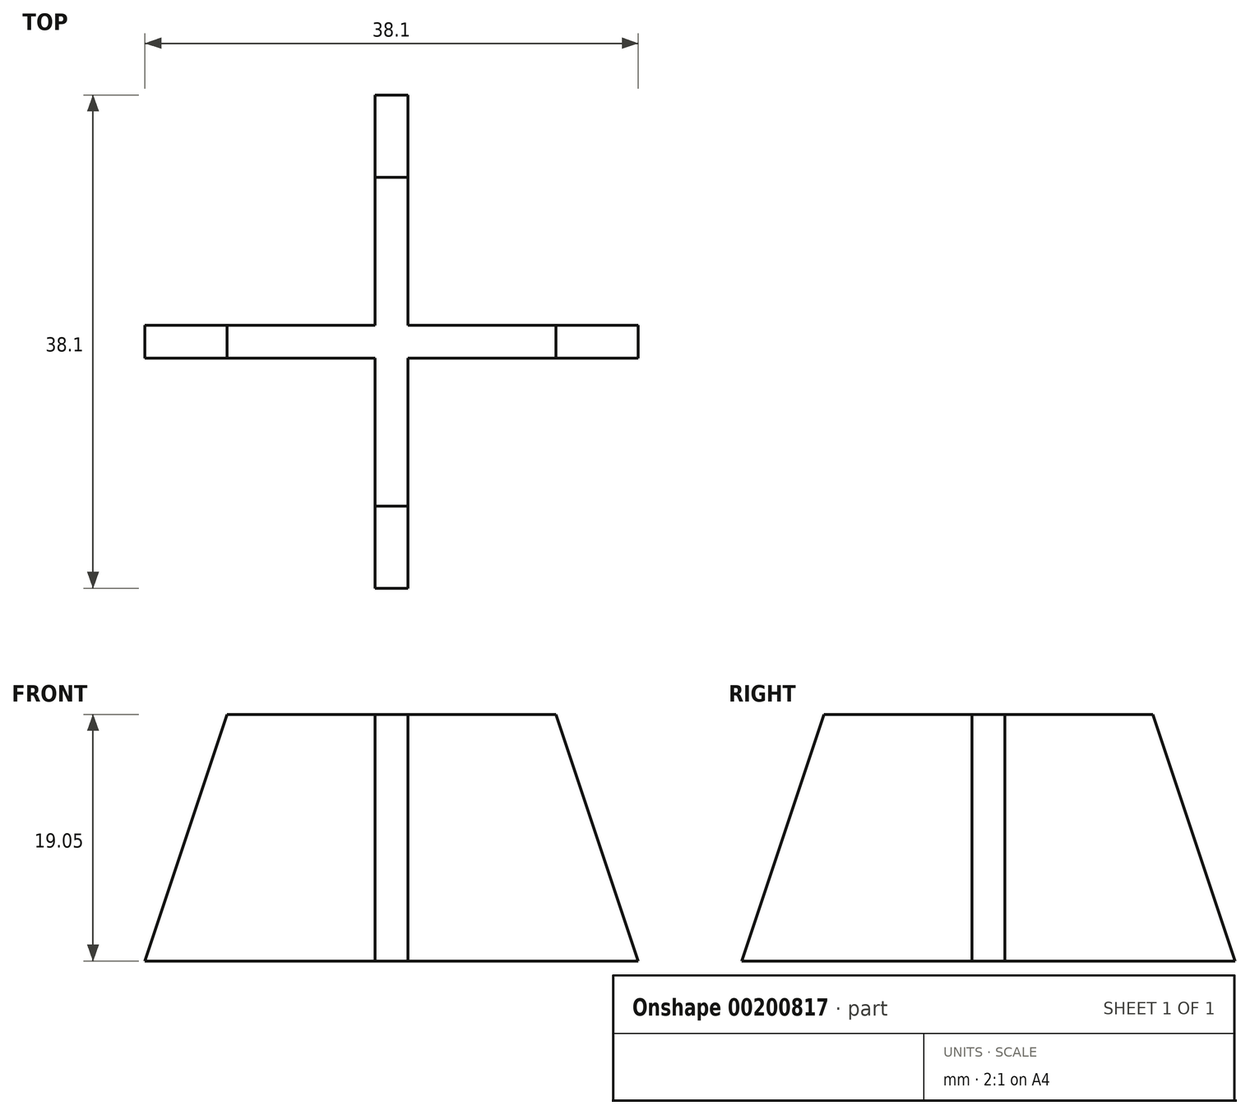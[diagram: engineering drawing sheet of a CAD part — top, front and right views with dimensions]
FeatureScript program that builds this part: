
annotation { "Feature Type Name" : "Feature", "Feature Type Description" : "" }
export const myFeature = defineFeature(function(context is Context, id is Id, definition is map)
    precondition{}
    {
        {
            var Q0;
            Q0=qCreatedBy(makeId("Top.planeOp"),FACE);
            var sketch = newSketch(context, id + "F0", { "sketchPlane" : qUnion([Q0])});
            skLineSegment(sketch, "E0.bottom", {"start": v(1.27, 19.05) * mm, "end": v(-1.27, 19.05) * mm});
            skLineSegment(sketch, "E0.top", {"start": v(1.27, -19.05) * mm, "end": v(-1.27, -19.05) * mm});
            skLineSegment(sketch, "E0.left", {"start": v(1.27, 19.05) * mm, "end": v(1.27, -19.05) * mm});
            skLineSegment(sketch, "E0.right", {"start": v(-1.27, 19.05) * mm, "end": v(-1.27, -19.05) * mm});
            skPoint(sketch, "E0.middle", {"position": v(0, 0) * mm});
            skLineSegment(sketch, "E1.bottom", {"start": v(-19.05, -1.27) * mm, "end": v(19.05, -1.27) * mm});
            skLineSegment(sketch, "E1.top", {"start": v(-19.05, 1.27) * mm, "end": v(19.05, 1.27) * mm});
            skLineSegment(sketch, "E1.left", {"start": v(-19.05, -1.27) * mm, "end": v(-19.05, 1.27) * mm});
            skLineSegment(sketch, "E1.right", {"start": v(19.05, -1.27) * mm, "end": v(19.05, 1.27) * mm});
            skSolve(sketch);
        }
        {
            var Q0;
            Q0=qCreatedBy(makeId("Top.planeOp"),FACE);
            cPlane(context, id + "F1", {"entities" : qUnion([Q0]), "cplaneType" : CPlaneType.OFFSET, "offset" : 19.05 * mm, "width" : 152.4 * mm, "height" : 152.4 * mm});
        }
        {
            var Q0;
            Q0=qCreatedBy(id+"F1.planeOp",FACE);
            var sketch = newSketch(context, id + "F2", { "sketchPlane" : qUnion([Q0])});
            skLineSegment(sketch, "E2.bottom", {"start": v(1.27, 12.7) * mm, "end": v(-1.27, 12.7) * mm});
            skLineSegment(sketch, "E2.top", {"start": v(1.27, -12.7) * mm, "end": v(-1.27, -12.7) * mm});
            skLineSegment(sketch, "E2.left", {"start": v(1.27, 12.7) * mm, "end": v(1.27, -12.7) * mm});
            skLineSegment(sketch, "E2.right", {"start": v(-1.27, 12.7) * mm, "end": v(-1.27, -12.7) * mm});
            skPoint(sketch, "E2.middle", {"position": v(0, 0) * mm});
            skLineSegment(sketch, "E3.bottom", {"start": v(-12.7, 1.27) * mm, "end": v(12.7, 1.27) * mm});
            skLineSegment(sketch, "E3.top", {"start": v(-12.7, -1.27) * mm, "end": v(12.7, -1.27) * mm});
            skLineSegment(sketch, "E3.left", {"start": v(-12.7, 1.27) * mm, "end": v(-12.7, -1.27) * mm});
            skLineSegment(sketch, "E3.right", {"start": v(12.7, 1.27) * mm, "end": v(12.7, -1.27) * mm});
            skSolve(sketch);
        }
        {
            var Q0;
            Q0 = qSketchRegion(id + "F0", true);
            var Q1;
            Q1 = qSketchRegion(id + "F2", true);
            loft(context, id + "F3", {"sheetProfilesArray" : [{ "sheetProfileEntities" : qUnion([Q0]) }, { "sheetProfileEntities" : qUnion([Q1]) }]});
        }
    });
